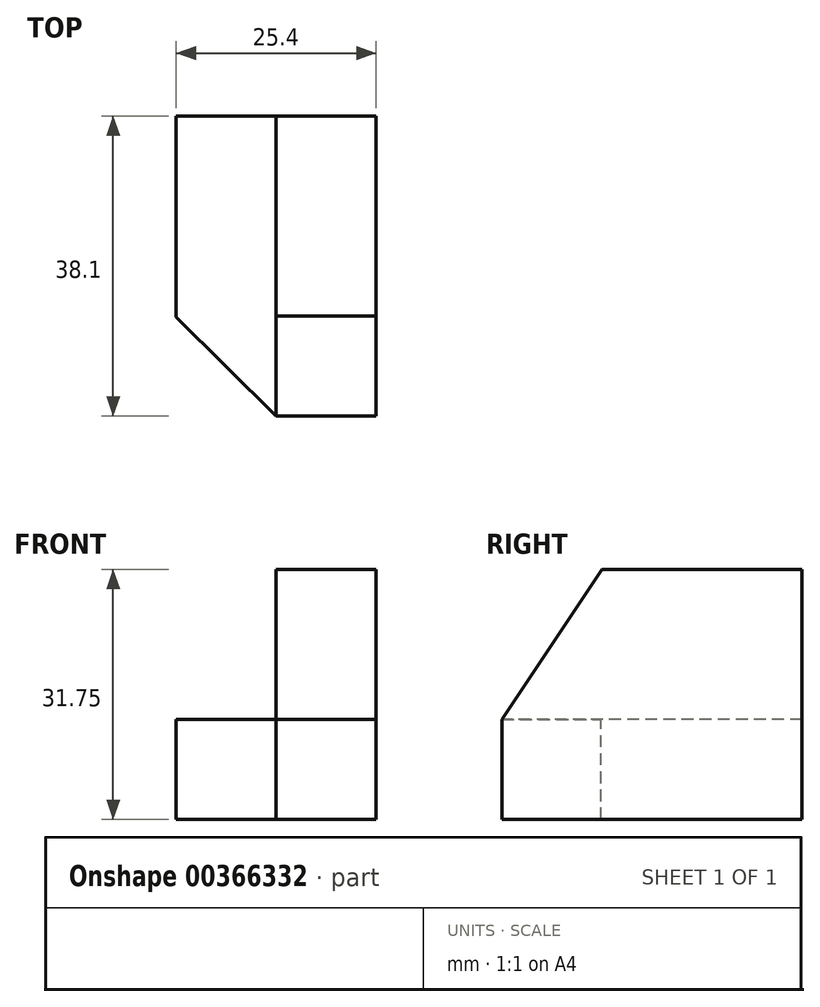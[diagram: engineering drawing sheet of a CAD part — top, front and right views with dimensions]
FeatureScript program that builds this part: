
annotation { "Feature Type Name" : "Feature", "Feature Type Description" : "" }
export const myFeature = defineFeature(function(context is Context, id is Id, definition is map)
    precondition{}
    {
        {
            var Q0;
            Q0=qCreatedBy(makeId("Front.planeOp"),FACE);
            var sketch = newSketch(context, id + "F0", { "sketchPlane" : qUnion([Q0])});
            skLineSegment(sketch, "E0", {"start": v(0, 12.7) * mm, "end": v(0, 0) * mm});
            skLineSegment(sketch, "E1", {"start": v(0, 0) * mm, "end": v(12.7, 0) * mm});
            skLineSegment(sketch, "E2", {"start": v(12.7, 0) * mm, "end": v(12.7, 12.7) * mm});
            skLineSegment(sketch, "E3", {"start": v(12.7, 12.7) * mm, "end": v(0, 12.7) * mm});
            skSolve(sketch);
        }
        {
            var Q0;
            Q0 = qSketchRegion(id + "F0", true);
            extrude(context, id + "F1", {"entities" : qUnion([Q0]), "depth" : 38.1 * mm});
        }
        {
            var Q0;
            Q0=makeQuery(id+"F1.opExtrude","SWEPT_FACE",FACE,{"disambiguationData":[OSD([sQuery(id+"F0.wireOp",EDGE,"E0")])]});
            var sketch = newSketch(context, id + "F2", { "sketchPlane" : qUnion([Q0])});
            skLineSegment(sketch, "E4", {"start": v(38.1, 12.7) * mm, "end": v(25.4, 31.75) * mm});
            skLineSegment(sketch, "E5", {"start": v(25.4, 31.75) * mm, "end": v(0, 31.75) * mm});
            skLineSegment(sketch, "E6", {"start": v(0, 31.75) * mm, "end": v(0, 12.7) * mm});
            skLineSegment(sketch, "E7", {"start": v(0, 12.7) * mm, "end": v(38.1, 12.7) * mm});
            skSolve(sketch);
        }
        {
            var Q0;
            Q0 = qSketchRegion(id + "F2", true);
            extrude(context, id + "F3", {"entities" : qUnion([Q0]), "operationType" : NewBodyOperationType.ADD, "oppositeDirection" : true, "depth" : 12.7 * mm});
        }
        {
            var Q0;
            Q0=makeQuery(id+"F1.opExtrude","CAP_FACE",FACE,{"disambiguationData":[OSD([sQuery(id+"F0.wireOp",EDGE,"E0"),sQuery(id+"F0.wireOp",EDGE,"E1"),sQuery(id+"F0.wireOp",EDGE,"E2"),sQuery(id+"F0.wireOp",EDGE,"E3")])],"isStart":false});
            var sketch = newSketch(context, id + "F4", { "sketchPlane" : qUnion([Q0])});
            skLineSegment(sketch, "E8", {"start": v(0, 12.7) * mm, "end": v(-12.7, 12.7) * mm});
            skLineSegment(sketch, "E9", {"start": v(-12.7, 12.7) * mm, "end": v(-12.7, 0) * mm});
            skLineSegment(sketch, "E10", {"start": v(-12.7, 0) * mm, "end": v(0, 0) * mm});
            skLineSegment(sketch, "E11", {"start": v(0, 0) * mm, "end": v(0, 12.7) * mm});
            skSolve(sketch);
        }
        {
            var Q0;
            Q0 = qSketchRegion(id + "F4", true);
            extrude(context, id + "F5", {"entities" : qUnion([Q0]), "operationType" : NewBodyOperationType.ADD, "oppositeDirection" : true, "depth" : 38.1 * mm});
        }
        {
            var Q0;
            Q0=makeQuery(id+"F5.opExtrude","SWEPT_FACE",FACE,{"disambiguationData":[OSD([sQuery(id+"F4.wireOp",EDGE,"E8")])]});
            var sketch = newSketch(context, id + "F6", { "sketchPlane" : qUnion([Q0])});
            skLineSegment(sketch, "E12", {"start": v(0, -38.1) * mm, "end": v(-12.7, -25.53) * mm});
            skSolve(sketch);
        }
        {
            var Q0;
            Q0 = qSketchRegion(id + "F6", true);
            var Q1;
            {var subQ0=sQuery(id+"F6.wireOp",EDGE,"E12");Q1=makeQuery(id+"F6.imprint","IMPRINT",FACE,{"disambiguationData":[TD([[makeQuery(id+"F6.imprint","IMPRINT",EDGE,{"derivedFrom":subQ0}),1.0]])]});}
            extrude(context, id + "F7", {"entities" : qUnion([Q0, Q1]), "operationType" : NewBodyOperationType.REMOVE, "oppositeDirection" : true, "depth" : 25.4 * mm});
        }
    });
